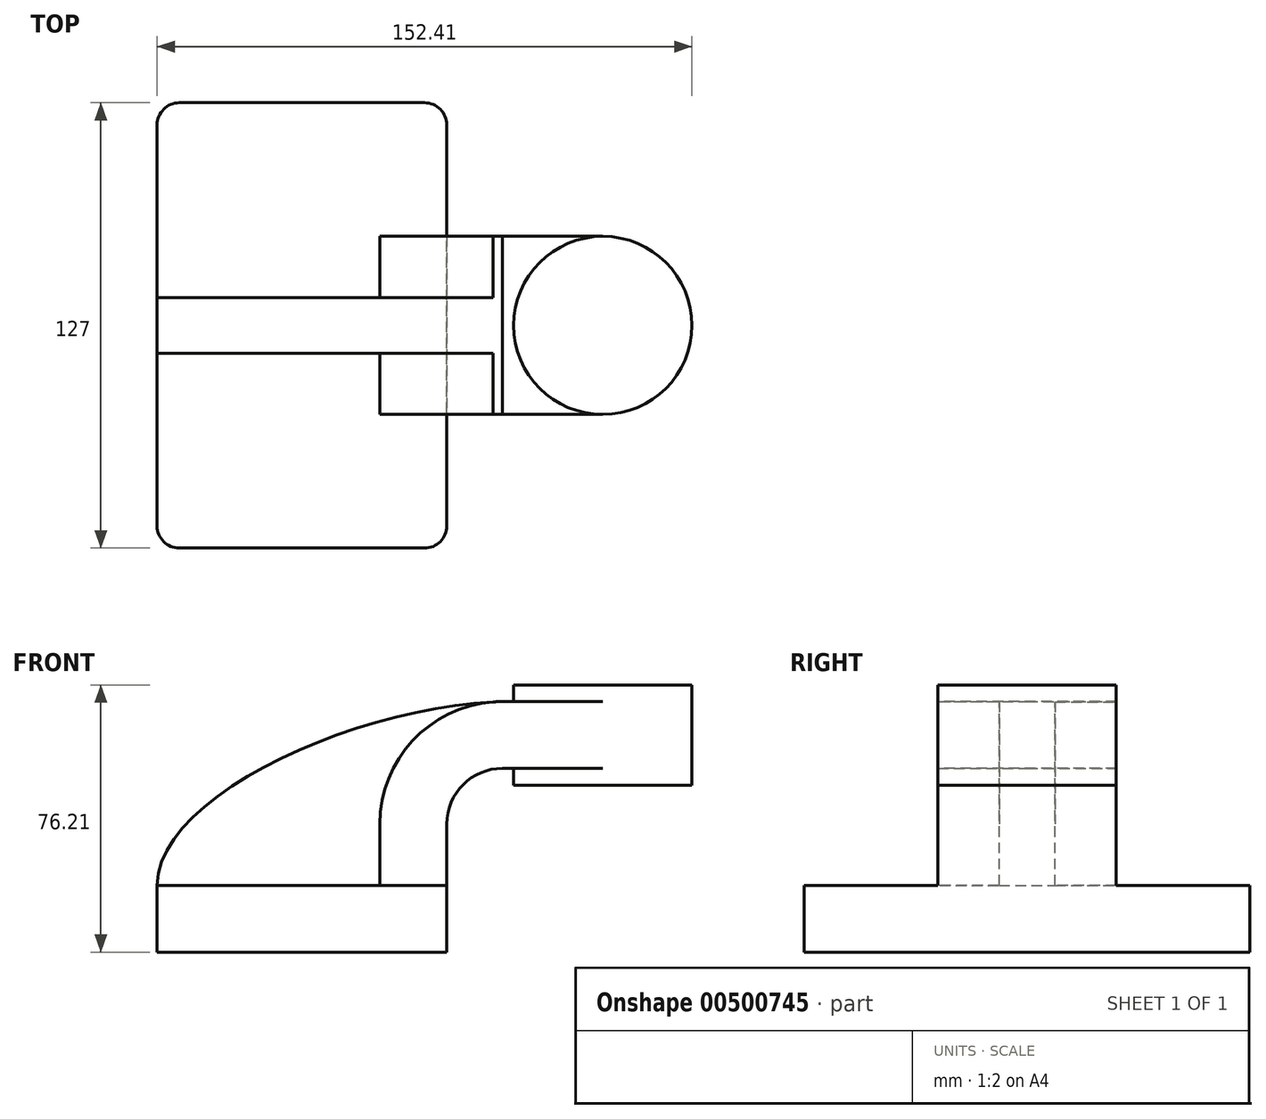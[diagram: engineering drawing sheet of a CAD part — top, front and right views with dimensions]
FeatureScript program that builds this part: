
annotation { "Feature Type Name" : "Feature", "Feature Type Description" : "" }
export const myFeature = defineFeature(function(context is Context, id is Id, definition is map)
    precondition{}
    {
        {
            var Q0;
            Q0=qCreatedBy(makeId("Front.planeOp"),FACE);
            var sketch = newSketch(context, id + "F0", { "sketchPlane" : qUnion([Q0])});
            skLineSegment(sketch, "E0.bottom", {"start": v(-41.28, -9.53) * mm, "end": v(41.28, -9.53) * mm});
            skLineSegment(sketch, "E0.top", {"start": v(-41.28, 9.53) * mm, "end": v(41.28, 9.53) * mm});
            skLineSegment(sketch, "E0.left", {"start": v(-41.28, -9.53) * mm, "end": v(-41.28, 9.53) * mm});
            skLineSegment(sketch, "E0.right", {"start": v(41.28, -9.53) * mm, "end": v(41.28, 9.53) * mm});
            skPoint(sketch, "E0.middle", {"position": v(0, 0) * mm});
            skLineSegment(sketch, "E1.bottom", {"start": v(60.33, 38.1) * mm, "end": v(111.12, 38.1) * mm});
            skLineSegment(sketch, "E1.top", {"start": v(60.33, 66.67) * mm, "end": v(111.12, 66.67) * mm});
            skLineSegment(sketch, "E1.left", {"start": v(60.33, 38.1) * mm, "end": v(60.33, 66.67) * mm});
            skLineSegment(sketch, "E1.right", {"start": v(111.12, 38.1) * mm, "end": v(111.12, 66.67) * mm});
            skPoint(sketch, "E1.middle", {"position": v(85.72, 52.39) * mm});
            skLineSegment(sketch, "E2", {"start": v(41.28, 9.53) * mm, "end": v(41.28, 27) * mm});
            skArc(sketch, "E3", {"start": v(41.27, 27) * mm, "mid": v(45.92, 38.23) * mm, "end": v(57.15, 42.88) * mm});
            skLineSegment(sketch, "E4", {"start": v(57.15, 42.88) * mm, "end": v(85.72, 42.88) * mm});
            skLineSegment(sketch, "E5", {"start": v(85.72, 38.1) * mm, "end": v(85.72, 66.67) * mm});
            skLineSegment(sketch, "E6.0", {"start": v(57.15, 61.93) * mm, "end": v(85.72, 61.93) * mm});
            skArc(sketch, "E6.1", {"start": v(22.23, 27) * mm, "mid": v(32.45, 51.7) * mm, "end": v(57.15, 61.93) * mm});
            skLineSegment(sketch, "E6.2", {"start": v(22.22, 9.53) * mm, "end": v(22.22, 27) * mm});
            skFitSpline(sketch, "E7", {"points": [v(-41.28, 9.53) * mm, v(57.15, 61.93) * mm], "startDerivative": vector(0.99, 78.17) * mm, "endDerivative": vector(122.04, 3.17) * mm});
            skSolve(sketch);
        }
        {
            var Q0;
            Q0=makeQuery(id+"F0.imprint","IMPRINT",FACE,{"disambiguationData":[TD([[makeQuery(id+"F0.imprint","IMPRINT",EDGE,{"derivedFrom":sQuery(id+"F0.wireOp",EDGE,"E0.bottom")}),1.0]])]});
            extrude(context, id + "F1", {"entities" : qUnion([Q0]), "endBound" : BoundingType.SYMMETRIC, "depth" : 127 * mm});
        }
        {
            var Q0;
            {var subQ0=sQuery(id+"F0.wireOp",EDGE,"E4");var subQ1=sQuery(id+"F0.wireOp",EDGE,"E1.left");var subQ2=makeQuery(id+"F0.imprint","INTERSECT",VERTEX,{"derivedFrom":[subQ1,subQ0]});Q0=makeQuery(id+"F0.imprint","IMPRINT",FACE,{"disambiguationData":[TD([[makeQuery(id+"F0.imprint","IMPRINT",EDGE,{"disambiguationData":[TD([[subQ2,-1.0]])],"derivedFrom":subQ1}),-1.0]])]});}
            var Q1;
            {var subQ1=sQuery(id+"F0.wireOp",EDGE,"E2");Q1=makeQuery(id+"F0.imprint","IMPRINT",FACE,{"disambiguationData":[TD([[makeQuery(id+"F0.imprint","IMPRINT",EDGE,{"derivedFrom":subQ1}),1.0]])]});}
            extrude(context, id + "F2", {"entities" : qUnion([Q0, Q1]), "operationType" : NewBodyOperationType.ADD, "endBound" : BoundingType.SYMMETRIC, "oppositeDirection" : true, "depth" : 50.8 * mm});
        }
        {
            var Q0;
            {var subQ3=sQuery(id+"F0.wireOp",EDGE,"E6.2");Q0=makeQuery(id+"F0.imprint","IMPRINT",FACE,{"disambiguationData":[TD([[makeQuery(id+"F0.imprint","IMPRINT",EDGE,{"derivedFrom":subQ3}),1.0]])]});}
            extrude(context, id + "F3", {"entities" : qUnion([Q0]), "operationType" : NewBodyOperationType.ADD, "endBound" : BoundingType.SYMMETRIC, "depth" : 15.88 * mm});
        }
        {
            var Q0;
            {var subQ4=sQuery(id+"F0.wireOp",EDGE,"E1.right");Q0=makeQuery(id+"F0.imprint","IMPRINT",FACE,{"disambiguationData":[TD([[makeQuery(id+"F0.imprint","IMPRINT",EDGE,{"derivedFrom":subQ4}),1.0]])]});}
            var Q1;
            Q1=sQuery(id+"F0.wireOp",EDGE,"E5");
            revolve(context, id + "F4", {"operationType" : NewBodyOperationType.ADD, "entities" : qUnion([Q0]), "axis" : qUnion([Q1]), "revolveType" : RevolveType.FULL});
        }
        {
            var Q0;
            Q0=makeQuery(id+"F1.opExtrude","CAP_EDGE",EDGE,{"disambiguationData":[OSD([sQuery(id+"F0.wireOp",EDGE,"E0.right")])],"isStart":false});
            var Q1;
            Q1=makeQuery(id+"F1.opExtrude","CAP_EDGE",EDGE,{"disambiguationData":[OSD([sQuery(id+"F0.wireOp",EDGE,"E0.left")])],"isStart":false});
            var Q2;
            Q2=makeQuery(id+"F1.opExtrude","CAP_EDGE",EDGE,{"disambiguationData":[OSD([sQuery(id+"F0.wireOp",EDGE,"E0.left")])],"isStart":true});
            var Q3;
            Q3=makeQuery(id+"F1.opExtrude","CAP_EDGE",EDGE,{"disambiguationData":[OSD([sQuery(id+"F0.wireOp",EDGE,"E0.right")])],"isStart":true});
            fillet(context, id + "F5", {"entities" : qUnion([Q0, Q1, Q2, Q3]), "radius" : 6.35 * mm, "tangentPropagation" : true, "allowEdgeOverflow" : false});
        }
    });
